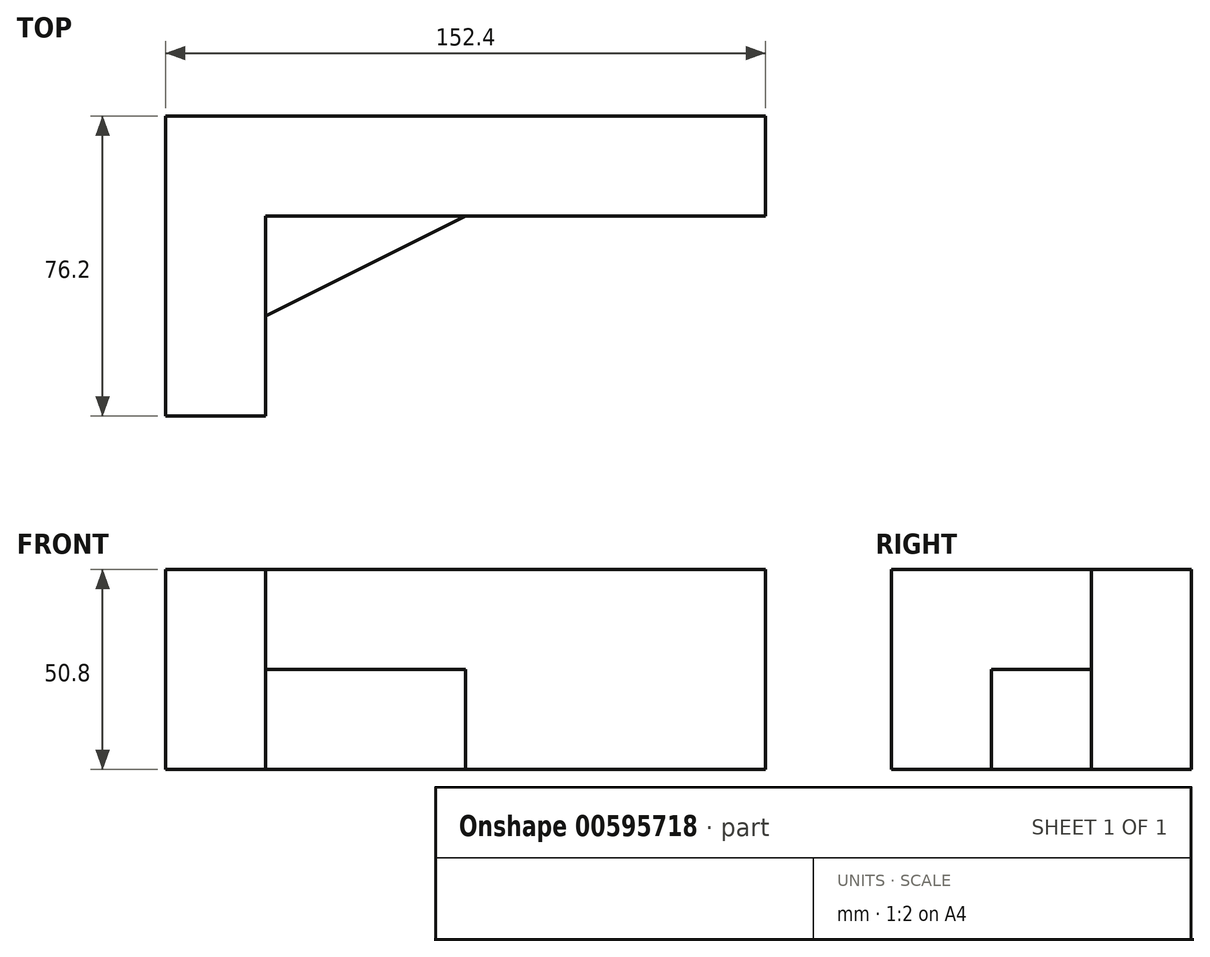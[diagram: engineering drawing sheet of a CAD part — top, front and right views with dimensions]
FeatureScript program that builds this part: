
annotation { "Feature Type Name" : "Feature", "Feature Type Description" : "" }
export const myFeature = defineFeature(function(context is Context, id is Id, definition is map)
    precondition{}
    {
        {
            var Q0;
            Q0=qCreatedBy(makeId("Top.planeOp"),FACE);
            var sketch = newSketch(context, id + "F0", { "sketchPlane" : qUnion([Q0])});
            skLineSegment(sketch, "E0", {"start": v(0, 0) * mm, "end": v(0, 76.2) * mm});
            skLineSegment(sketch, "E1", {"start": v(0, 76.2) * mm, "end": v(152.4, 76.2) * mm});
            skLineSegment(sketch, "E2", {"start": v(152.4, 76.2) * mm, "end": v(152.4, 0) * mm});
            skLineSegment(sketch, "E3", {"start": v(152.4, 0) * mm, "end": v(0, 0) * mm});
            skSolve(sketch);
        }
        {
            var Q0;
            Q0=makeQuery(id+"F0.imprint","IMPRINT",FACE,{"disambiguationData":[TD([[makeQuery(id+"F0.imprint","IMPRINT",EDGE,{"derivedFrom":sQuery(id+"F0.wireOp",EDGE,"E0")}),-1.0]])]});
            extrude(context, id + "F1", {"entities" : qUnion([Q0]), "depth" : 50.8 * mm, "offsetDistance" : 25.4 * mm});
        }
        {
            var Q0;
            Q0=makeQuery(id+"F1.opExtrude","CAP_FACE",FACE,{"disambiguationData":[OSD([sQuery(id+"F0.wireOp",EDGE,"E0"),sQuery(id+"F0.wireOp",EDGE,"E1"),sQuery(id+"F0.wireOp",EDGE,"E2"),sQuery(id+"F0.wireOp",EDGE,"E3")])],"isStart":false});
            var sketch = newSketch(context, id + "F2", { "sketchPlane" : qUnion([Q0])});
            skLineSegment(sketch, "E4", {"start": v(152.4, 76.2) * mm, "end": v(152.4, 50.8) * mm});
            skLineSegment(sketch, "E5", {"start": v(152.4, 50.8) * mm, "end": v(25.4, 50.8) * mm});
            skLineSegment(sketch, "E6", {"start": v(25.4, 50.8) * mm, "end": v(25.4, 0) * mm});
            skLineSegment(sketch, "E7", {"start": v(25.4, 0) * mm, "end": v(152.4, 0) * mm});
            skLineSegment(sketch, "E8", {"start": v(152.4, 0) * mm, "end": v(152.4, 50.8) * mm});
            skSolve(sketch);
        }
        {
            var Q0;
            Q0=makeQuery(id+"F2.imprint","IMPRINT",FACE,{"disambiguationData":[TD([[makeQuery(id+"F2.imprint","IMPRINT",EDGE,{"derivedFrom":sQuery(id+"F2.wireOp",EDGE,"E5")}),1.0]])]});
            extrude(context, id + "F3", {"entities" : qUnion([Q0]), "operationType" : NewBodyOperationType.REMOVE, "oppositeDirection" : true, "depth" : 25.4 * mm, "offsetDistance" : 25.4 * mm});
        }
        {
            var Q0;
            Q0=makeQuery(id+"F3.boolean.opBoolean","COPY",FACE,{"derivedFrom":makeQuery(id+"F3.opExtrude","CAP_FACE",FACE,{"disambiguationData":[OSD([sQuery(id+"F2.wireOp",EDGE,"E5"),sQuery(id+"F2.wireOp",EDGE,"E6"),sQuery(id+"F2.wireOp",EDGE,"E7"),sQuery(id+"F2.wireOp",EDGE,"E8")])],"isStart":false})});
            var sketch = newSketch(context, id + "F4", { "sketchPlane" : qUnion([Q0])});
            skLineSegment(sketch, "E9", {"start": v(76.2, 50.8) * mm, "end": v(25.4, 25.4) * mm});
            skLineSegment(sketch, "E10", {"start": v(25.4, 25.4) * mm, "end": v(25.4, 0) * mm});
            skLineSegment(sketch, "E11", {"start": v(25.4, 0) * mm, "end": v(152.4, 0) * mm});
            skLineSegment(sketch, "E12", {"start": v(152.4, 0) * mm, "end": v(152.4, 50.8) * mm});
            skLineSegment(sketch, "E13", {"start": v(152.4, 50.8) * mm, "end": v(76.2, 50.8) * mm});
            skSolve(sketch);
        }
        {
            var Q0;
            Q0=makeQuery(id+"F4.imprint","IMPRINT",FACE,{"disambiguationData":[TD([[makeQuery(id+"F4.imprint","IMPRINT",EDGE,{"derivedFrom":sQuery(id+"F4.wireOp",EDGE,"E9")}),1.0]])]});
            extrude(context, id + "F5", {"entities" : qUnion([Q0]), "operationType" : NewBodyOperationType.REMOVE, "oppositeDirection" : true, "depth" : 25.4 * mm, "offsetDistance" : 25.4 * mm});
        }
    });
